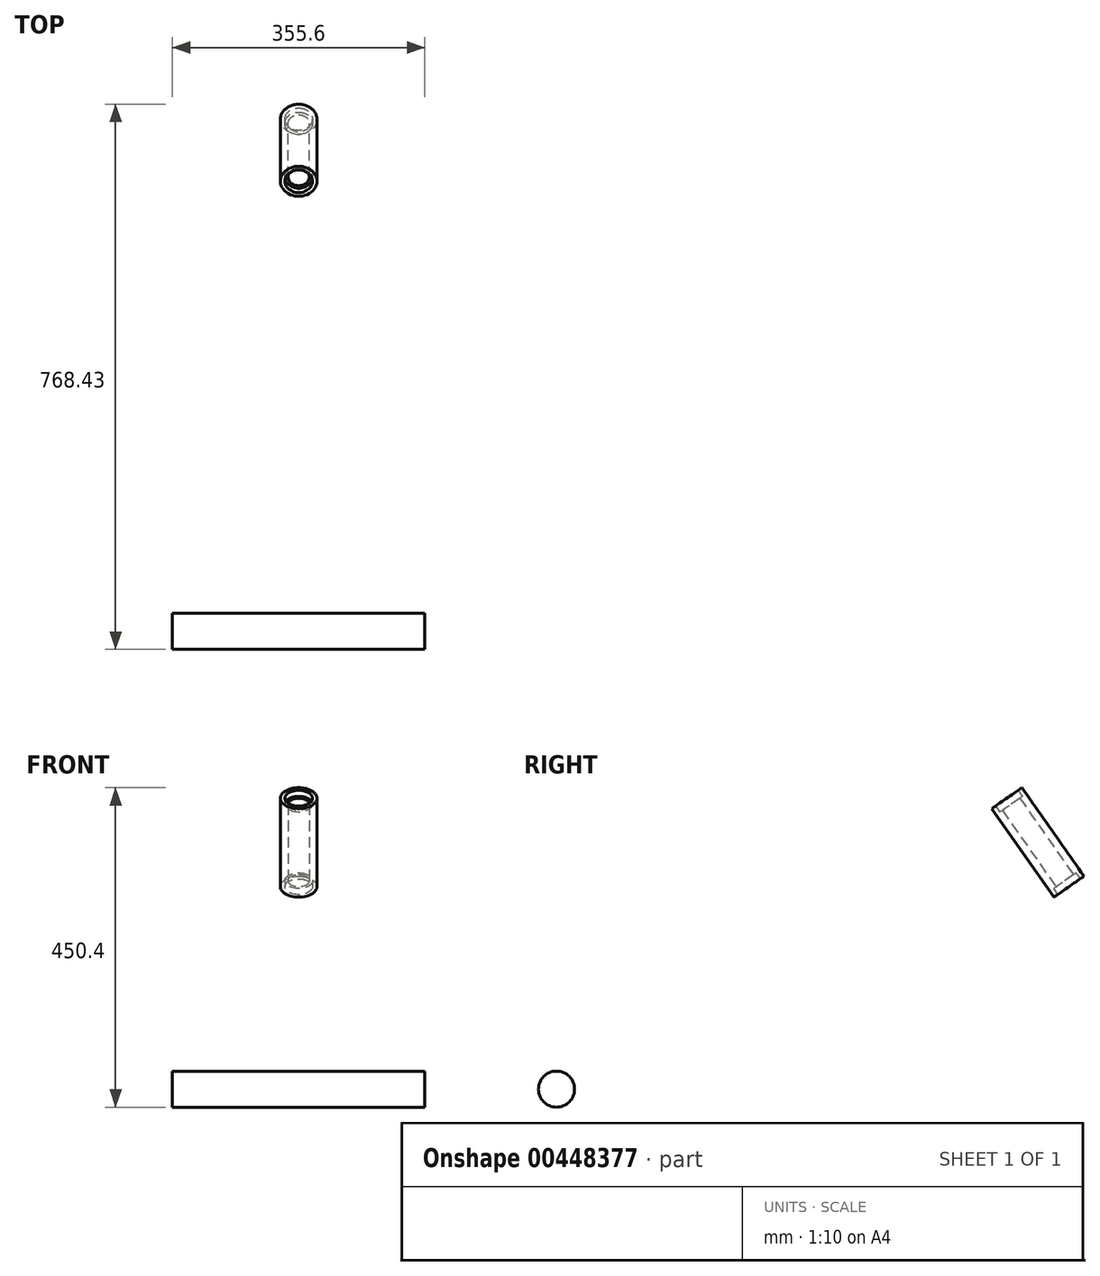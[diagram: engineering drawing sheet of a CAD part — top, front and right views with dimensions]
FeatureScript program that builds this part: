
annotation { "Feature Type Name" : "Feature", "Feature Type Description" : "" }
export const myFeature = defineFeature(function(context is Context, id is Id, definition is map)
    precondition{}
    {
        {
            var Q0;
            Q0=qCreatedBy(makeId("Right.planeOp"),FACE);
            var sketch = newSketch(context, id + "F0", { "sketchPlane" : qUnion([Q0])});
            skCircle(sketch, "E0", {"center": v(0, 0) * mm, "radius": 25.4 * mm});
            skLineSegment(sketch, "E1", {"start": v(-762, 0) * mm, "end": v(1016, 0) * mm});
            skCircle(sketch, "E2", {"center": v(-762, 0) * mm, "radius": 241.3 * mm});
            skCircle(sketch, "E3", {"center": v(1016, 0) * mm, "radius": 241.3 * mm});
            skLineSegment(sketch, "E4", {"start": v(-44.7, 196.88) * mm, "end": v(-241.8, 196.88) * mm});
            skLineSegment(sketch, "E5", {"start": v(1030.02, -240.9) * mm, "end": v(-761.95, -241.3) * mm});
            skLineSegment(sketch, "E6", {"start": v(1016, 0) * mm, "end": v(1016, 479.9) * mm});
            skLineSegment(sketch, "E7", {"start": v(1016, 0) * mm, "end": v(667.38, 497.89) * mm});
            skLineSegment(sketch, "E8", {"start": v(655.62, 425) * mm, "end": v(743.03, 300.16) * mm});
            skLineSegment(sketch, "E9", {"start": v(743.03, 300.16) * mm, "end": v(737.83, 296.52) * mm});
            skLineSegment(sketch, "E10", {"start": v(721.92, 285.38) * mm, "end": v(634.5, 410.22) * mm});
            skLineSegment(sketch, "E11", {"start": v(650.42, 421.36) * mm, "end": v(655.62, 425) * mm});
            skLineSegment(sketch, "E12", {"start": v(650.42, 421.36) * mm, "end": v(656.43, 412.77) * mm});
            skLineSegment(sketch, "E13", {"start": v(656.43, 412.77) * mm, "end": v(652.8, 410.22) * mm});
            skLineSegment(sketch, "E14", {"start": v(652.8, 410.22) * mm, "end": v(728.28, 302.41) * mm});
            skLineSegment(sketch, "E15", {"start": v(728.28, 302.41) * mm, "end": v(731.92, 304.96) * mm});
            skLineSegment(sketch, "E16", {"start": v(731.92, 304.96) * mm, "end": v(737.83, 296.52) * mm});
            skSolve(sketch);
        }
        {
            var Q0;
            Q0=makeQuery(id+"F0.imprint","IMPRINT",FACE,{"disambiguationData":[TD([[makeQuery(id+"F0.imprint","IMPRINT",EDGE,{"derivedFrom":sQuery(id+"F0.wireOp",EDGE,"E8")}),-1.0]])]});
            var Q1;
            Q1=sQuery(id+"F0.wireOp",EDGE,"E10");
            revolve(context, id + "F1", {"entities" : qUnion([Q0]), "axis" : qUnion([Q1]), "revolveType" : RevolveType.FULL});
        }
        {
            var Q0;
            {var subQ0=sQuery(id+"F0.wireOp",EDGE,"E1");var subQ1=sQuery(id+"F0.wireOp",EDGE,"E0");var subQ2=makeQuery(id+"F0.imprint","INTERSECT",VERTEX,{"disambiguationData":[OD(0.0)],"derivedFrom":[subQ1,subQ0]});Q0=makeQuery(id+"F0.imprint","IMPRINT",FACE,{"disambiguationData":[TD([[makeQuery(id+"F0.imprint","IMPRINT",EDGE,{"disambiguationData":[TD([[subQ2,1.0]])],"derivedFrom":subQ1}),1.0]])]});}
            var Q1;
            {var subQ0=sQuery(id+"F0.wireOp",EDGE,"E1");var subQ1=sQuery(id+"F0.wireOp",EDGE,"E0");var subQ2=makeQuery(id+"F0.imprint","INTERSECT",VERTEX,{"disambiguationData":[OD(0.0)],"derivedFrom":[subQ1,subQ0]});Q1=makeQuery(id+"F0.imprint","IMPRINT",FACE,{"disambiguationData":[TD([[makeQuery(id+"F0.imprint","IMPRINT",EDGE,{"disambiguationData":[TD([[subQ2,-1.0]])],"derivedFrom":subQ1}),1.0]])]});}
            extrude(context, id + "F2", {"entities" : qUnion([Q0, Q1]), "endBound" : BoundingType.SYMMETRIC, "depth" : 355.6 * mm, "offsetDistance" : 25.4 * mm});
        }
    });
